# Revit family: EZTS
name_source: partatom
category: Mechanical Equipment
revit_build: Autodesk Revit 2018 (Build: 20170223_1515(x64)
units: mm (PartAtom-declared; Revit-internal decimal feet)

## family parameters
Always vertical = Yes
Cut with Voids When Loaded = No
OmniClass Number = 23.75.00.00
OmniClass Title = Climate Control (HVAC)
Part Type = Normal
Room Calculation Point = No
Round Connector Dimension = Use Diameter
Shared = No
Work Plane-Based = No

## types (18) — shared parameters
Description = EZTS With Controller
Discharge = 0' - 0 5/8"
EnclosureFront = 0' - 3"
EnclosureHeight = 0' - 11 3/32"
EnclosureWidth = 0' - 7 1/8"
EnslosureRear = 1' - 2 7/32"
Inlet_S = 0' - 5 3/8"
Manufacturer = ANEMOSTAT PRODUCTS
Model = EZTS

## per-type parameters (varying)
| type | DischargeX | DischargeY | EnclosureCenter | Height | InletDia | InletRadius | LeftController | Length | RightController | URL | Width |
| Inlet Size 06 W/ Controller LH | 0' - 8 3/4" | 0' - 8 3/4" | 0' - 5" | 0' - 10" | 0' - 5 7/8" | 0' - 2 15/16" | Yes | 1' - 0 1/2" | No | https://www.anemostat-hvac.com | 0' - 10" |
| Inlet Size 06 W/ Controller RH | 0' - 8 3/4" | 0' - 8 3/4" | 0' - 5" | 0' - 10" | 0' - 5 7/8" | 0' - 2 15/16" | No | 1' - 0 1/2" | Yes | https://www.anemostat-hvac.com | 0' - 10" |
| Inlet Size 05 W/ Controller LH | 0' - 8 3/4" | 0' - 8 3/4" | 0' - 5" | 0' - 10" | 0' - 4 7/8" | 0' - 2 7/16" | Yes | 1' - 0 1/2" | No | https://www.anemostat-hvac.com | 0' - 10" |
| Inlet Size 05 W/ Controller RH | 0' - 8 3/4" | 0' - 8 3/4" | 0' - 5" | 0' - 10" | 0' - 4 7/8" | 0' - 2 7/16" | No | 1' - 0 1/2" | Yes | https://www.anemostat-hvac.com | 0' - 10" |
| Inlet Size 08 W/ Controller LH | 0' - 10 3/4" | 0' - 8 3/4" | 0' - 5" | 0' - 10" | 0' - 7 7/8" | 0' - 3 15/16" | Yes | 1' - 0 1/2" | No | https://www.anemostat-hvac.com | 1' - 0" |
| Inlet Size 08 W/ Controller RH | 0' - 10 3/4" | 0' - 8 3/4" | 0' - 5" | 0' - 10" | 0' - 7 7/8" | 0' - 3 15/16" | No | 1' - 0 1/2" | Yes | https://www.anemostat-hvac.com | 1' - 0" |
| Inlet Size 07 W/ Controller RH | 0' - 10 3/4" | 0' - 8 3/4" | 0' - 5" | 0' - 10" | 0' - 6 7/8" | 0' - 3 7/16" | No | 1' - 0 1/2" | Yes | https://www.anemostat-hvac.com | 1' - 0" |
| Inlet Size 07 W/ Controller LH | 0' - 10 3/4" | 0' - 8 3/4" | 0' - 5" | 0' - 10" | 0' - 6 7/8" | 0' - 3 7/16" | Yes | 1' - 0 1/2" | No | https://www.anemostat-hvac.com | 1' - 0" |
| Inlet Size 10 W/ Controller LH | 1' - 0 3/4" | 0' - 11 1/4" | 0' - 6 1/4" | 1' - 0 1/2" | 0' - 9 7/8" | 0' - 4 15/16" | Yes | 1' - 2 1/2" | No | https://www.anemostat-hvac.com | 1' - 2" |
| Inlet Size 10 W/ Controller RH | 1' - 0 3/4" | 0' - 11 1/4" | 0' - 6 1/4" | 1' - 0 1/2" | 0' - 9 7/8" | 0' - 4 15/16" | No | 1' - 2 1/2" | Yes | https://www.anemostat-hvac.com | 1' - 2" |
| Inlet Size 09 W/ Controller RH | 1' - 0 3/4" | 0' - 11 1/4" | 0' - 6 1/4" | 1' - 0 1/2" | 0' - 8 7/8" | 0' - 4 7/16" | No | 1' - 2 1/2" | Yes | https://www.anemostat-hvac.com | 1' - 2" |
| Inlet Size 09 W/ Controller LH | 1' - 0 3/4" | 0' - 11 1/4" | 0' - 6 1/4" | 1' - 0 1/2" | 0' - 8 7/8" | 0' - 4 7/16" | Yes | 1' - 2 1/2" | No | https://www.anemostat-hvac.com | 1' - 2" |
| Inlet Size 12 W/ Controller LH | 1' - 2 3/4" | 1' - 1 3/4" | 0' - 7 1/2" | 1' - 3" | 0' - 11 7/8" | 0' - 5 15/16" | Yes | 1' - 6 1/2" | No | https://www.anemostat-hvac.com | 1' - 4" |
| Inlet Size 12 W/ Controller RH | 1' - 2 3/4" | 1' - 1 3/4" | 0' - 7 1/2" | 1' - 3" | 0' - 11 7/8" | 0' - 5 15/16" | No | 1' - 6 1/2" | Yes | https://www.anemostat-hvac.com | 1' - 4" |
| Inlet Size 14 W/ Controller LH | 1' - 6 3/4" | 1' - 4 1/4" | 0' - 8 3/4" | 1' - 5 1/2" | 1' - 1 7/8" | 0' - 6 15/16" | Yes | 1' - 6 1/2" | No | https://www.anemostat-hvac.com | 1' - 8" |
| Inlet Size 14 W/ Controller RH | 1' - 6 3/4" | 1' - 4 1/4" | 0' - 8 3/4" | 1' - 5 1/2" | 1' - 1 7/8" | 0' - 6 15/16" | No | 1' - 6 1/2" | Yes | https://www.anemostat-hvac.com | 1' - 8" |
| Inlet Size 16 W/ Controller LH | 1' - 10 3/4" | 1' - 4 1/4" | 0' - 8 3/4" | 1' - 5 1/2" | 1' - 3 7/8" | 0' - 7 15/16" | Yes | 1' - 6 1/2" | No | https://www.anemostat-hvac.com | 2' - 0" |
| Inlet Size 16 W/ Controller RH | 1' - 10 3/4" | 1' - 4 1/4" | 0' - 8 3/4" | 1' - 5 1/2" | 1' - 3 7/8" | 0' - 7 15/16" | No | 1' - 6 1/2" | Yes | https://www.anemostat-hvac.com
https://www.anemostat-hvac.com
https://www.anemostat-hvac.com | 2' - 0" |

## geometry (parser evidence)
native form markers: Sweep x3
no freeform markers — native parametric forms only
